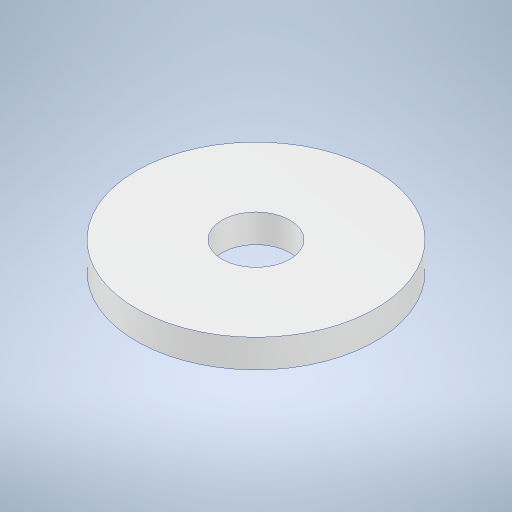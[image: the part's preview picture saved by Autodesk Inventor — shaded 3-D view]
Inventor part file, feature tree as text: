
AUTODESK INVENTOR PART (.ipt)
format: ipt  version: 2023.2 (Build 272271000, 271)  size: 240,640 bytes
history: native  units: in
note: dims shown in document units (in); Inventor stores cm internally (conversion verified against a paired STEP export)
features: extrude x1, sketch x1
ambient origin geometry x8: Origin, YZ Plane, XZ Plane, XY Plane, X Axis, Y Axis, Z Axis, Center Point
bodies: Solid1 (feature_tree)
feature tree (2):
  extrude  "Extrusion1"  Depth=0.1024in
  sketch  "Sketch1"  dims[d0=0.8661in d1=0.2461in d2=0.1024in d3=0.0in]
